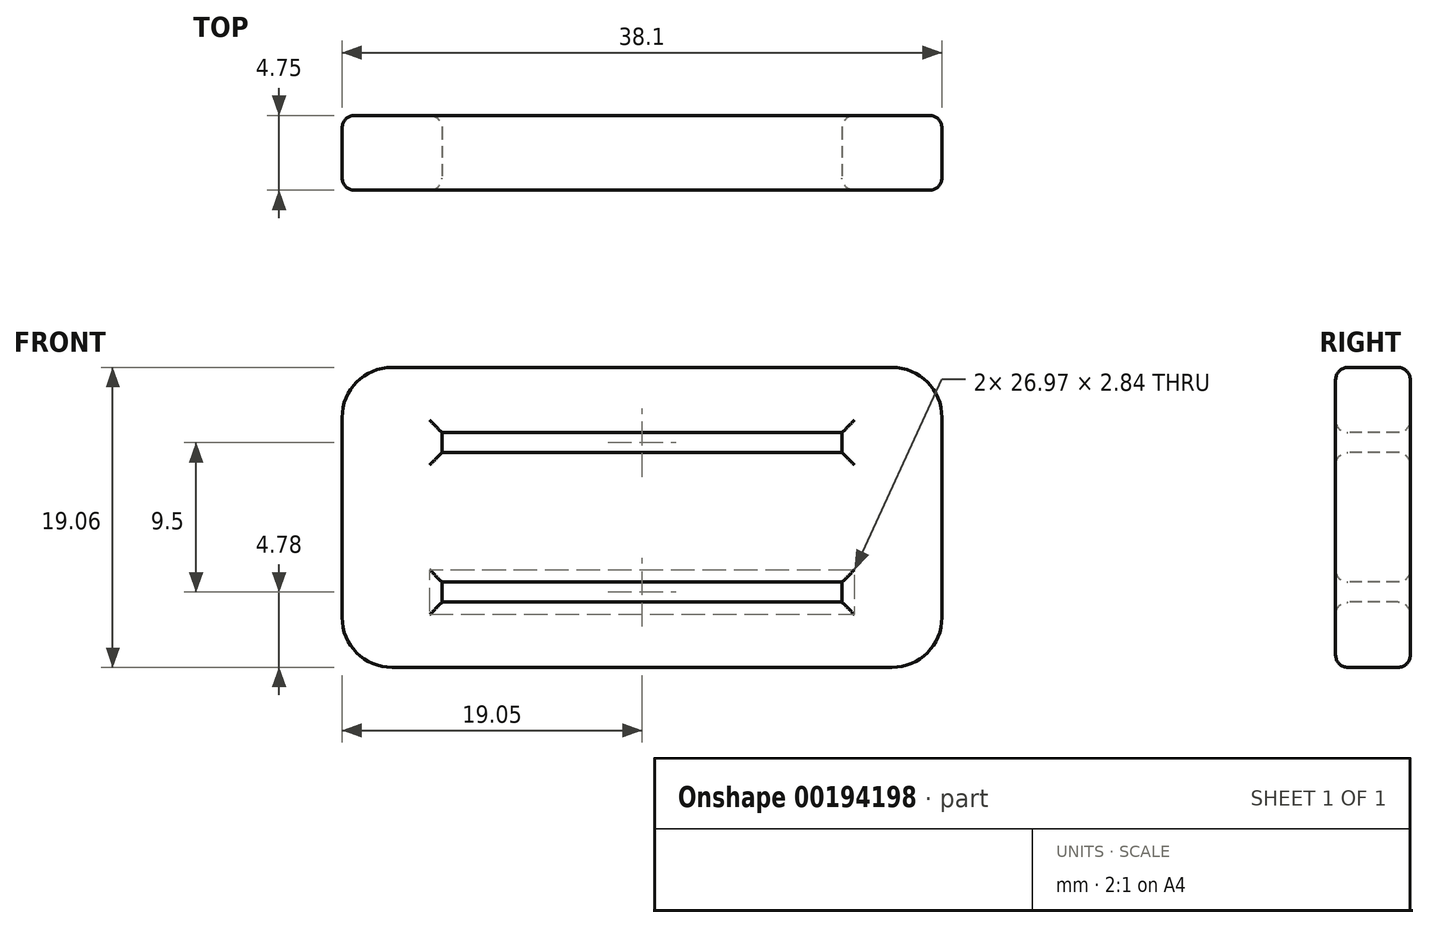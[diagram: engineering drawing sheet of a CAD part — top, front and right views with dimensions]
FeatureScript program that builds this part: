
annotation { "Feature Type Name" : "Feature", "Feature Type Description" : "" }
export const myFeature = defineFeature(function(context is Context, id is Id, definition is map)
    precondition{}
    {
        {
            var Q0;
            Q0=qCreatedBy(makeId("Front.planeOp"),FACE);
            var sketch = newSketch(context, id + "F0", { "sketchPlane" : qUnion([Q0])});
            skLineSegment(sketch, "E0.bottom", {"start": v(19.05, 9.53) * mm, "end": v(-19.05, 9.53) * mm});
            skLineSegment(sketch, "E0.top", {"start": v(19.05, -9.53) * mm, "end": v(-19.05, -9.53) * mm});
            skLineSegment(sketch, "E0.left", {"start": v(19.05, 9.52) * mm, "end": v(19.05, -9.53) * mm});
            skLineSegment(sketch, "E0.right", {"start": v(-19.05, 9.53) * mm, "end": v(-19.05, -9.53) * mm});
            skPoint(sketch, "E0.middle", {"position": v(0, 0) * mm});
            skLineSegment(sketch, "E1.bottom", {"start": v(-12.7, 4.11) * mm, "end": v(12.7, 4.11) * mm});
            skLineSegment(sketch, "E1.top", {"start": v(-12.7, 5.38) * mm, "end": v(12.7, 5.38) * mm});
            skLineSegment(sketch, "E1.left", {"start": v(-12.7, 4.11) * mm, "end": v(-12.7, 5.38) * mm});
            skLineSegment(sketch, "E1.right", {"start": v(12.7, 4.11) * mm, "end": v(12.7, 5.38) * mm});
            skPoint(sketch, "E1.middle", {"position": v(0, 4.75) * mm});
            skLineSegment(sketch, "E2", {"start": v(-19.05, 0) * mm, "end": v(19.05, 0) * mm, "construction": true});
            skLineSegment(sketch, "E3.MirrorCS", {"start": v(-12.7, -4.11) * mm, "end": v(12.7, -4.11) * mm});
            skLineSegment(sketch, "E4.MirrorCS", {"start": v(-12.7, -4.11) * mm, "end": v(-12.7, -5.38) * mm});
            skLineSegment(sketch, "E5.MirrorCS", {"start": v(-12.7, -5.38) * mm, "end": v(12.7, -5.38) * mm});
            skLineSegment(sketch, "E6.MirrorCS", {"start": v(12.7, -4.11) * mm, "end": v(12.7, -5.38) * mm});
            skSolve(sketch);
        }
        {
            var Q0;
            Q0=makeQuery(id+"F0.imprint","IMPRINT",FACE,{"disambiguationData":[TD([[makeQuery(id+"F0.imprint","IMPRINT",EDGE,{"derivedFrom":sQuery(id+"F0.wireOp",EDGE,"E0.bottom")}),1.0]])]});
            extrude(context, id + "F1", {"entities" : qUnion([Q0]), "oppositeDirection" : true, "depth" : 4.75 * mm});
        }
        {
            var Q0;
            Q0=makeQuery(id+"F1.opExtrude","SWEPT_EDGE",EDGE,{"disambiguationData":[OSD([sQuery(id+"F0.wireOp",EDGE,"E0.bottom"),sQuery(id+"F0.wireOp",EDGE,"E0.left")])]});
            var Q1;
            Q1=makeQuery(id+"F1.opExtrude","SWEPT_EDGE",EDGE,{"disambiguationData":[OSD([sQuery(id+"F0.wireOp",EDGE,"E0.top"),sQuery(id+"F0.wireOp",EDGE,"E0.left")])]});
            var Q2;
            Q2=makeQuery(id+"F1.opExtrude","SWEPT_EDGE",EDGE,{"disambiguationData":[OSD([sQuery(id+"F0.wireOp",EDGE,"E0.bottom"),sQuery(id+"F0.wireOp",EDGE,"E0.right")])]});
            var Q3;
            Q3=makeQuery(id+"F1.opExtrude","SWEPT_EDGE",EDGE,{"disambiguationData":[OSD([sQuery(id+"F0.wireOp",EDGE,"E0.top"),sQuery(id+"F0.wireOp",EDGE,"E0.right")])]});
            fillet(context, id + "F2", {"entities" : qUnion([Q0, Q1, Q2, Q3]), "radius" : 3.17 * mm, "tangentPropagation" : true, "allowEdgeOverflow" : false});
        }
        {
            var Q0;
            Q0=makeQuery(id+"F1.opExtrude","CAP_FACE",FACE,{"disambiguationData":[OSD([sQuery(id+"F0.wireOp",EDGE,"E0.bottom"),sQuery(id+"F0.wireOp",EDGE,"E0.top"),sQuery(id+"F0.wireOp",EDGE,"E0.left"),sQuery(id+"F0.wireOp",EDGE,"E0.right"),sQuery(id+"F0.wireOp",EDGE,"E1.bottom"),sQuery(id+"F0.wireOp",EDGE,"E1.top"),sQuery(id+"F0.wireOp",EDGE,"E1.left"),sQuery(id+"F0.wireOp",EDGE,"E1.right"),sQuery(id+"F0.wireOp",EDGE,"E3.MirrorCS"),sQuery(id+"F0.wireOp",EDGE,"E4.MirrorCS"),sQuery(id+"F0.wireOp",EDGE,"E5.MirrorCS"),sQuery(id+"F0.wireOp",EDGE,"E6.MirrorCS")])],"isStart":true});
            var Q1;
            Q1=makeQuery(id+"F1.opExtrude","CAP_FACE",FACE,{"disambiguationData":[OSD([sQuery(id+"F0.wireOp",EDGE,"E0.bottom"),sQuery(id+"F0.wireOp",EDGE,"E0.top"),sQuery(id+"F0.wireOp",EDGE,"E0.left"),sQuery(id+"F0.wireOp",EDGE,"E0.right"),sQuery(id+"F0.wireOp",EDGE,"E1.bottom"),sQuery(id+"F0.wireOp",EDGE,"E1.top"),sQuery(id+"F0.wireOp",EDGE,"E1.left"),sQuery(id+"F0.wireOp",EDGE,"E1.right"),sQuery(id+"F0.wireOp",EDGE,"E3.MirrorCS"),sQuery(id+"F0.wireOp",EDGE,"E4.MirrorCS"),sQuery(id+"F0.wireOp",EDGE,"E5.MirrorCS"),sQuery(id+"F0.wireOp",EDGE,"E6.MirrorCS")])],"isStart":false});
            fillet(context, id + "F3", {"entities" : qUnion([Q0, Q1]), "radius" : 0.79 * mm, "tangentPropagation" : true, "allowEdgeOverflow" : false});
        }
    });
